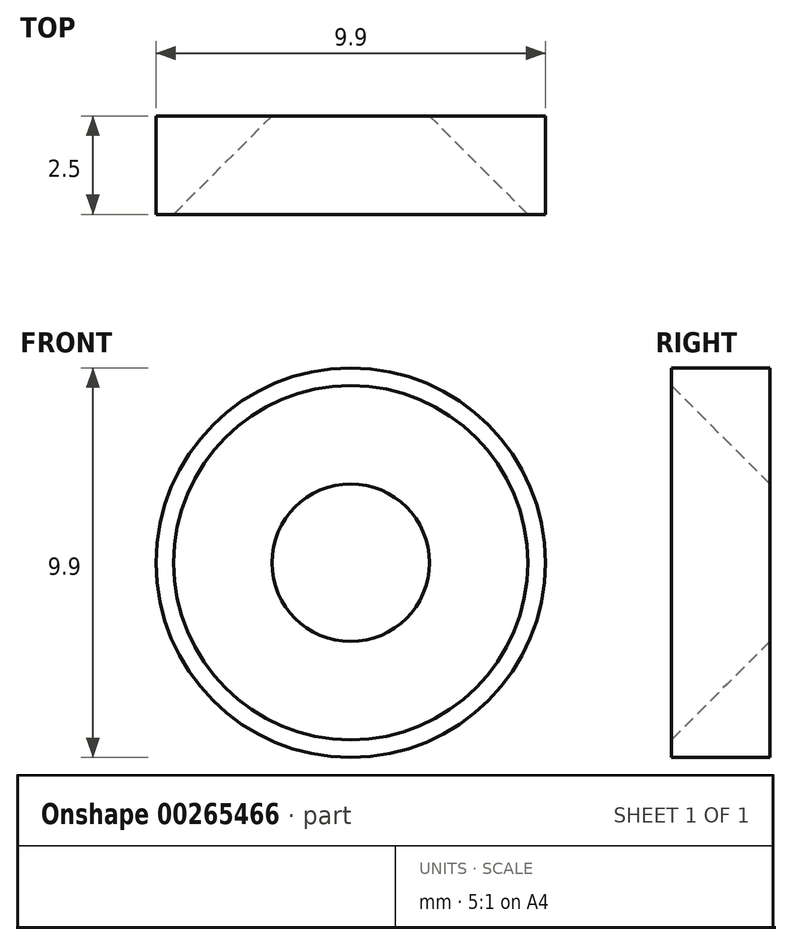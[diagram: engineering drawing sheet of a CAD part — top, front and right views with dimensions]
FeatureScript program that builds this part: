
annotation { "Feature Type Name" : "Feature", "Feature Type Description" : "" }
export const myFeature = defineFeature(function(context is Context, id is Id, definition is map)
    precondition{}
    {
        {
            var Q0;
            Q0=qCreatedBy(makeId("Front.planeOp"),FACE);
            var sketch = newSketch(context, id + "F0", { "sketchPlane" : qUnion([Q0])});
            skCircle(sketch, "E0", {"center": v(0, 0) * mm, "radius": 4.95 * mm});
            skCircle(sketch, "E1", {"center": v(0, 0) * mm, "radius": 3.85 * mm});
            skCircle(sketch, "E2", {"center": v(0, 0) * mm, "radius": 2 * mm});
            skSolve(sketch);
        }
        {
            var Q0;
            Q0=makeQuery(id+"F0.imprint","IMPRINT",FACE,{"disambiguationData":[TD([[makeQuery(id+"F0.imprint","IMPRINT",EDGE,{"derivedFrom":sQuery(id+"F0.wireOp",EDGE,"E0")}),1.0]])]});
            var Q1;
            Q1=makeQuery(id+"F0.imprint","IMPRINT",FACE,{"disambiguationData":[TD([[makeQuery(id+"F0.imprint","IMPRINT",EDGE,{"derivedFrom":sQuery(id+"F0.wireOp",EDGE,"E2")}),1.0]])]});
            var Q2;
            Q2=makeQuery(id+"F0.imprint","IMPRINT",FACE,{"disambiguationData":[TD([[makeQuery(id+"F0.imprint","IMPRINT",EDGE,{"derivedFrom":sQuery(id+"F0.wireOp",EDGE,"E1")}),1.0]])]});
            extrude(context, id + "F1", {"entities" : qUnion([Q0, Q1, Q2]), "depth" : 2.5 * mm});
        }
        {
            var Q0;
            Q0=makeQuery(id+"F0.imprint","IMPRINT",FACE,{"disambiguationData":[TD([[makeQuery(id+"F0.imprint","IMPRINT",EDGE,{"derivedFrom":sQuery(id+"F0.wireOp",EDGE,"E2")}),1.0]])]});
            var Q1;
            Q1=sQuery(id+"F0.wireOp",EDGE,"E2");
            extrude(context, id + "F2", {"entities" : qUnion([Q0]), "operationType" : NewBodyOperationType.REMOVE, "surfaceEntities" : qUnion([Q1]), "depth" : 3.19 * mm});
        }
        {
            var Q0;
            Q0=makeQuery(id+"F2.boolean.opBoolean","INTERSECT",EDGE,{"derivedFrom":[makeQuery(id+"F1.opExtrude","CAP_FACE",FACE,{"disambiguationData":[OSD([sQuery(id+"F0.wireOp",EDGE,"E0")])],"isStart":false}),makeQuery(id+"F2.opExtrude","SWEPT_FACE",FACE,{"disambiguationData":[OSD([sQuery(id+"F0.wireOp",EDGE,"E2")])]})]});
            chamfer(context, id + "F3", {"entities" : qUnion([Q0]), "chamferType" : ChamferType.OFFSET_ANGLE, "width" : 2.5 * mm, "oppositeDirection" : false, "angle" : 45 * degree, "tangentPropagation" : true});
        }
    });
